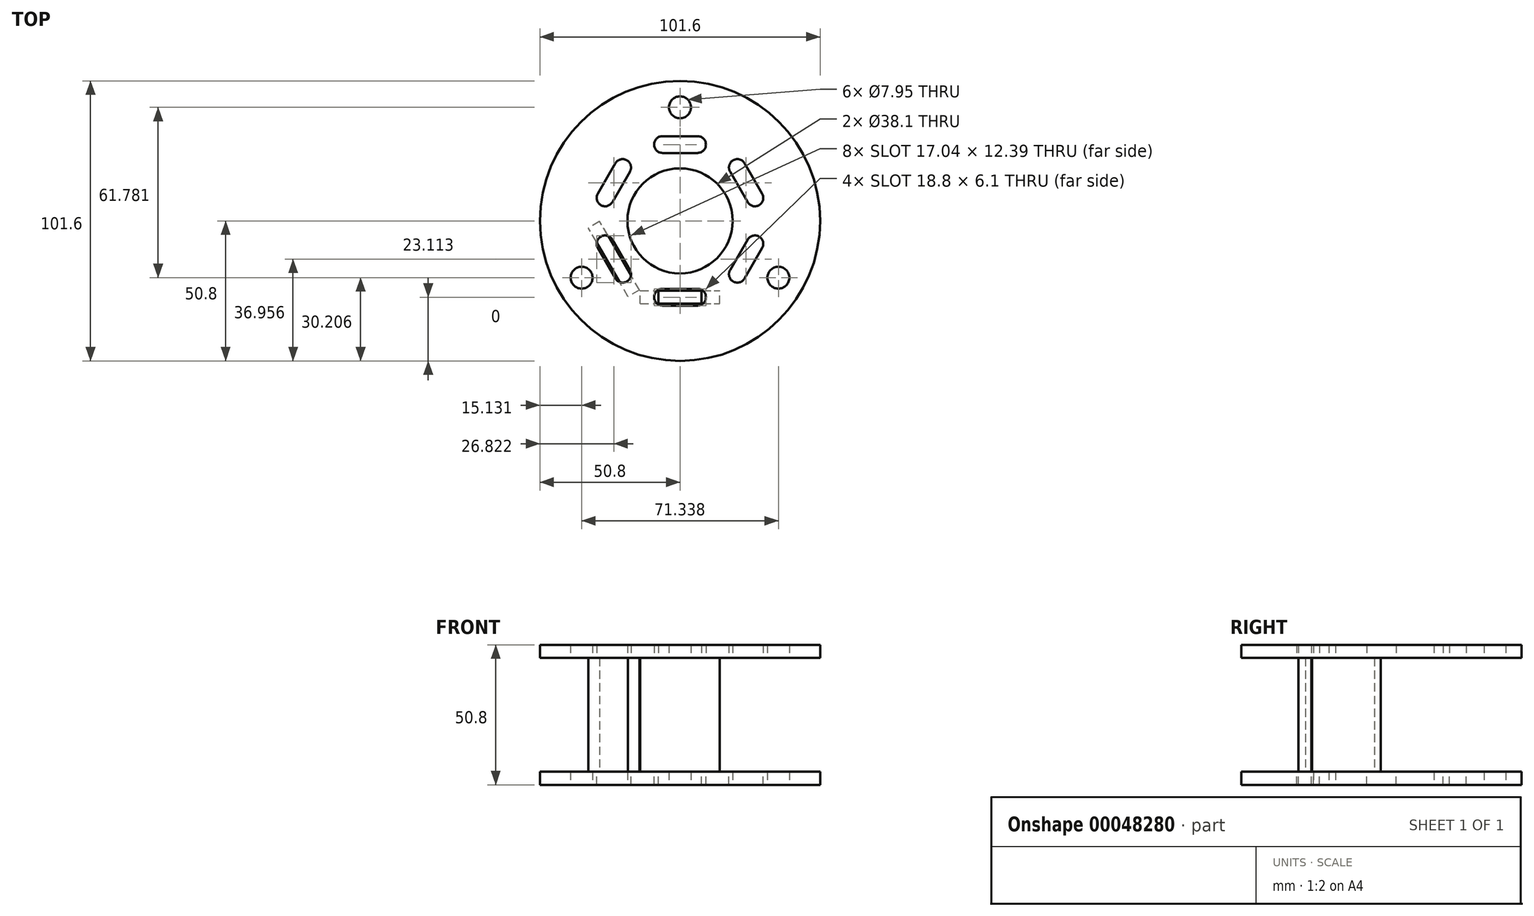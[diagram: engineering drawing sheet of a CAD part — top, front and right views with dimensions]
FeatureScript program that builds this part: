
annotation { "Feature Type Name" : "Feature", "Feature Type Description" : "" }
export const myFeature = defineFeature(function(context is Context, id is Id, definition is map)
    precondition{}
    {
        {
            var Q0;
            Q0=qCreatedBy(makeId("Top.planeOp"),FACE);
            var sketch = newSketch(context, id + "F0", { "sketchPlane" : qUnion([Q0])});
            skCircle(sketch, "E0", {"center": v(0, 0) * mm, "radius": 19.05 * mm});
            skCircle(sketch, "E1", {"center": v(0, 0) * mm, "radius": 50.8 * mm});
            skCircle(sketch, "E2", {"center": v(0, 41.19) * mm, "radius": 3.98 * mm});
            skCircle(sketch, "E3.1.0", {"center": v(-35.67, -20.6) * mm, "radius": 3.98 * mm});
            skCircle(sketch, "E3.2.0", {"center": v(35.67, -20.6) * mm, "radius": 3.98 * mm});
            skSolve(sketch);
        }
        {
            var Q0;
            Q0 = qSketchRegion(id + "F0", true);
            extrude(context, id + "F1", {"entities" : qUnion([Q0]), "depth" : 4.75 * mm});
        }
        {
            var Q0;
            Q0=makeQuery(id+"F1.opExtrude","CAP_FACE",FACE,{"disambiguationData":[OSD([sQuery(id+"F0.wireOp",EDGE,"E0"),sQuery(id+"F0.wireOp",EDGE,"E1"),sQuery(id+"F0.wireOp",EDGE,"E2"),sQuery(id+"F0.wireOp",EDGE,"E3.1.0"),sQuery(id+"F0.wireOp",EDGE,"E3.2.0")])],"isStart":false});
            var sketch = newSketch(context, id + "F2", { "sketchPlane" : qUnion([Q0])});
            skCircle(sketch, "E4.cCircle", {"center": v(0, 0) * mm, "radius": 27.69 * mm, "construction": true});
            skLineSegment(sketch, "E4.0", {"start": v(15.99, -27.69) * mm, "end": v(-15.99, -27.69) * mm, "construction": true});
            skLineSegment(sketch, "E4.1", {"start": v(-15.99, -27.69) * mm, "end": v(-31.97, 0) * mm, "construction": true});
            skLineSegment(sketch, "E4.2", {"start": v(-31.97, 0) * mm, "end": v(-15.99, 27.69) * mm, "construction": true});
            skLineSegment(sketch, "E4.3", {"start": v(-15.99, 27.69) * mm, "end": v(15.99, 27.69) * mm, "construction": true});
            skLineSegment(sketch, "E4.4", {"start": v(15.99, 27.69) * mm, "end": v(31.97, 0) * mm, "construction": true});
            skLineSegment(sketch, "E4.5", {"start": v(31.97, 0) * mm, "end": v(15.99, -27.69) * mm, "construction": true});
            skPoint(sketch, "E4.0.midPoint", {"position": v(0, -27.69) * mm});
            skSolve(sketch);
        }
        {
            var Q0;
            Q0=makeQuery(id+"F2.imprint","IMPRINT",FACE,{"disambiguationData":[TD([[makeQuery(id+"F2.imprint","IMPRINT",EDGE,{"derivedFrom":makeQuery(id+"F1.opExtrude","CAP_EDGE",EDGE,{"disambiguationData":[OSD([sQuery(id+"F0.wireOp",EDGE,"E0")])],"isStart":false})}),-1.0]])]});
            var sketch = newSketch(context, id + "F3", { "sketchPlane" : qUnion([Q0])});
            skPoint(sketch, "E5.0", {"position": v(0, -27.69) * mm});
            skPoint(sketch, "E5.1", {"position": v(23.98, 13.84) * mm});
            skPoint(sketch, "E5.2", {"position": v(0, 27.69) * mm});
            skPoint(sketch, "E5.3", {"position": v(-23.98, 13.84) * mm});
            skPoint(sketch, "E5.4", {"position": v(-23.98, -13.84) * mm});
            skPoint(sketch, "E5.5", {"position": v(23.98, -13.84) * mm});
            skLineSegment(sketch, "E6", {"start": v(-6.35, 27.69) * mm, "end": v(6.35, 27.69) * mm});
            skLineSegment(sketch, "E7", {"start": v(27.15, 8.34) * mm, "end": v(20.8, 19.34) * mm});
            skLineSegment(sketch, "E8", {"start": v(27.15, -8.34) * mm, "end": v(20.8, -19.34) * mm});
            skLineSegment(sketch, "E9", {"start": v(6.35, -27.69) * mm, "end": v(-6.35, -27.69) * mm});
            skLineSegment(sketch, "E10", {"start": v(-20.8, -19.34) * mm, "end": v(-27.15, -8.34) * mm});
            skLineSegment(sketch, "E11", {"start": v(-27.15, 8.34) * mm, "end": v(-20.8, 19.34) * mm});
            skArc(sketch, "E12.0.startCap", {"start": v(-6.35, 24.64) * mm, "mid": v(-9.4, 27.69) * mm, "end": v(-6.35, 30.73) * mm});
            skArc(sketch, "E12.0.endCap", {"start": v(6.35, 30.73) * mm, "mid": v(9.4, 27.69) * mm, "end": v(6.35, 24.64) * mm});
            skLineSegment(sketch, "E12.0.left", {"start": v(-6.35, 30.73) * mm, "end": v(6.35, 30.73) * mm});
            skLineSegment(sketch, "E12.0.right", {"start": v(-6.35, 24.64) * mm, "end": v(6.35, 24.64) * mm});
            skArc(sketch, "E12.1.startCap", {"start": v(29.8, 9.87) * mm, "mid": v(28.68, 5.7) * mm, "end": v(24.51, 6.82) * mm});
            skArc(sketch, "E12.1.endCap", {"start": v(18.16, 17.82) * mm, "mid": v(19.28, 21.98) * mm, "end": v(23.44, 20.87) * mm});
            skLineSegment(sketch, "E12.1.left", {"start": v(24.51, 6.82) * mm, "end": v(18.16, 17.82) * mm});
            skLineSegment(sketch, "E12.1.right", {"start": v(29.8, 9.87) * mm, "end": v(23.44, 20.87) * mm});
            skArc(sketch, "E12.2.startCap", {"start": v(24.51, -6.82) * mm, "mid": v(28.68, -5.7) * mm, "end": v(29.8, -9.87) * mm});
            skArc(sketch, "E12.2.endCap", {"start": v(23.44, -20.87) * mm, "mid": v(19.28, -21.98) * mm, "end": v(18.16, -17.82) * mm});
            skLineSegment(sketch, "E12.2.left", {"start": v(29.8, -9.87) * mm, "end": v(23.44, -20.87) * mm});
            skLineSegment(sketch, "E12.2.right", {"start": v(24.51, -6.82) * mm, "end": v(18.16, -17.82) * mm});
            skArc(sketch, "E12.3.startCap", {"start": v(6.35, -24.64) * mm, "mid": v(9.4, -27.69) * mm, "end": v(6.35, -30.73) * mm});
            skArc(sketch, "E12.3.endCap", {"start": v(-6.35, -30.73) * mm, "mid": v(-9.4, -27.69) * mm, "end": v(-6.35, -24.64) * mm});
            skLineSegment(sketch, "E12.3.left", {"start": v(6.35, -30.73) * mm, "end": v(-6.35, -30.73) * mm});
            skLineSegment(sketch, "E12.3.right", {"start": v(6.35, -24.64) * mm, "end": v(-6.35, -24.64) * mm});
            skArc(sketch, "E12.4.startCap", {"start": v(-18.16, -17.82) * mm, "mid": v(-19.28, -21.98) * mm, "end": v(-23.44, -20.87) * mm});
            skArc(sketch, "E12.4.endCap", {"start": v(-29.8, -9.87) * mm, "mid": v(-28.68, -5.7) * mm, "end": v(-24.51, -6.82) * mm});
            skLineSegment(sketch, "E12.4.left", {"start": v(-23.44, -20.87) * mm, "end": v(-29.8, -9.87) * mm});
            skLineSegment(sketch, "E12.4.right", {"start": v(-18.16, -17.82) * mm, "end": v(-24.51, -6.82) * mm});
            skArc(sketch, "E12.5.startCap", {"start": v(-24.51, 6.82) * mm, "mid": v(-28.68, 5.7) * mm, "end": v(-29.8, 9.87) * mm});
            skArc(sketch, "E12.5.endCap", {"start": v(-23.44, 20.87) * mm, "mid": v(-19.28, 21.98) * mm, "end": v(-18.16, 17.82) * mm});
            skLineSegment(sketch, "E12.5.left", {"start": v(-29.8, 9.87) * mm, "end": v(-23.44, 20.87) * mm});
            skLineSegment(sketch, "E12.5.right", {"start": v(-24.51, 6.82) * mm, "end": v(-18.16, 17.82) * mm});
            skSolve(sketch);
        }
        {
            var Q0;
            Q0 = qSketchRegion(id + "F3", true);
            extrude(context, id + "F4", {"entities" : qUnion([Q0]), "operationType" : NewBodyOperationType.REMOVE, "oppositeDirection" : true, "depth" : 25.4 * mm});
        }
        {
            var Q0;
            Q0=makeQuery(id+"F2.imprint","IMPRINT",FACE,{"disambiguationData":[TD([[makeQuery(id+"F2.imprint","IMPRINT",EDGE,{"derivedFrom":makeQuery(id+"F1.opExtrude","CAP_EDGE",EDGE,{"disambiguationData":[OSD([sQuery(id+"F0.wireOp",EDGE,"E0")])],"isStart":false})}),-1.0]])]});
            var sketch = newSketch(context, id + "F5", { "sketchPlane" : qUnion([Q0])});
            skPoint(sketch, "E13.0", {"position": v(0, -27.69) * mm});
            skPoint(sketch, "E13.1", {"position": v(23.98, -13.84) * mm});
            skPoint(sketch, "E13.2", {"position": v(23.98, 13.84) * mm});
            skPoint(sketch, "E13.3", {"position": v(0, 27.69) * mm});
            skPoint(sketch, "E13.4", {"position": v(-23.98, 13.84) * mm});
            skPoint(sketch, "E13.5", {"position": v(-23.98, -13.84) * mm});
            skLineSegment(sketch, "E14.bottom", {"start": v(-14.4, -30.06) * mm, "end": v(14.4, -30.06) * mm});
            skLineSegment(sketch, "E14.top", {"start": v(-14.4, -25.31) * mm, "end": v(14.4, -25.31) * mm});
            skLineSegment(sketch, "E14.left", {"start": v(-14.4, -30.06) * mm, "end": v(-14.4, -25.31) * mm});
            skLineSegment(sketch, "E14.right", {"start": v(14.4, -30.06) * mm, "end": v(14.4, -25.31) * mm});
            skPoint(sketch, "E15.0", {"position": v(-15.99, -27.69) * mm});
            skLineSegment(sketch, "E16.bottom", {"start": v(-14.72, -25.12) * mm, "end": v(-18.84, -27.5) * mm});
            skLineSegment(sketch, "E16.top", {"start": v(-29.12, -0.19) * mm, "end": v(-33.23, -2.56) * mm});
            skLineSegment(sketch, "E16.left", {"start": v(-14.72, -25.12) * mm, "end": v(-29.12, -0.19) * mm});
            skLineSegment(sketch, "E16.right", {"start": v(-18.84, -27.5) * mm, "end": v(-33.23, -2.56) * mm});
            skSolve(sketch);
        }
        {
            var Q0;
            Q0 = qSketchRegion(id + "F5", true);
            extrude(context, id + "F6", {"entities" : qUnion([Q0]), "depth" : 41.3 * mm});
        }
        {
            var Q0;
            Q0=makeQuery(id+"F6.opExtrude","CAP_FACE",FACE,{"disambiguationData":[OSD([sQuery(id+"F5.wireOp",EDGE,"E14.bottom"),sQuery(id+"F5.wireOp",EDGE,"E14.top"),sQuery(id+"F5.wireOp",EDGE,"E14.left"),sQuery(id+"F5.wireOp",EDGE,"E14.right")])],"isStart":true});
            var sketch = newSketch(context, id + "F7", { "sketchPlane" : qUnion([Q0])});
            skPoint(sketch, "E17.0", {"position": v(9.4, 27.69) * mm});
            skPoint(sketch, "E17.1", {"position": v(-9.4, 27.69) * mm});
            skLineSegment(sketch, "E18", {"start": v(-7.81, 27.69) * mm, "end": v(7.81, 27.69) * mm, "construction": true});
            skPoint(sketch, "E19", {"position": v(0, 27.69) * mm});
            skLineSegment(sketch, "E20.bottom", {"start": v(7.81, 25.31) * mm, "end": v(-7.81, 25.31) * mm});
            skLineSegment(sketch, "E20.top", {"start": v(7.81, 30.06) * mm, "end": v(-7.81, 30.06) * mm});
            skLineSegment(sketch, "E20.left", {"start": v(7.81, 25.31) * mm, "end": v(7.81, 30.06) * mm});
            skLineSegment(sketch, "E20.right", {"start": v(-7.81, 25.31) * mm, "end": v(-7.81, 30.06) * mm});
            skSolve(sketch);
        }
        {
            var Q0;
            Q0 = qSketchRegion(id + "F7", true);
            extrude(context, id + "F8", {"entities" : qUnion([Q0]), "operationType" : NewBodyOperationType.ADD, "depth" : 4.75 * mm});
        }
        {
            var Q0;
            Q0=makeQuery(id+"F6.opExtrude","CAP_FACE",FACE,{"disambiguationData":[OSD([sQuery(id+"F5.wireOp",EDGE,"E14.bottom"),sQuery(id+"F5.wireOp",EDGE,"E14.top"),sQuery(id+"F5.wireOp",EDGE,"E14.left"),sQuery(id+"F5.wireOp",EDGE,"E14.right")])],"isStart":false});
            var sketch = newSketch(context, id + "F9", { "sketchPlane" : qUnion([Q0])});
            skLineSegment(sketch, "E21.0", {"start": v(29.8, -9.87) * mm, "end": v(23.44, -20.87) * mm});
            skArc(sketch, "E21.1", {"start": v(24.51, -6.82) * mm, "mid": v(28.68, -5.7) * mm, "end": v(29.8, -9.87) * mm});
            skLineSegment(sketch, "E21.2", {"start": v(24.51, -6.82) * mm, "end": v(18.16, -17.82) * mm});
            skArc(sketch, "E21.3", {"start": v(23.44, -20.87) * mm, "mid": v(19.28, -21.98) * mm, "end": v(18.16, -17.82) * mm});
            skLineSegment(sketch, "E21.4", {"start": v(24.51, 6.82) * mm, "end": v(18.16, 17.82) * mm});
            skArc(sketch, "E21.5", {"start": v(29.8, 9.87) * mm, "mid": v(28.68, 5.7) * mm, "end": v(24.51, 6.82) * mm});
            skLineSegment(sketch, "E21.6", {"start": v(29.8, 9.87) * mm, "end": v(23.44, 20.87) * mm});
            skArc(sketch, "E21.7", {"start": v(18.16, 17.82) * mm, "mid": v(19.28, 21.98) * mm, "end": v(23.44, 20.87) * mm});
            skArc(sketch, "E21.8", {"start": v(6.35, 30.73) * mm, "mid": v(9.4, 27.69) * mm, "end": v(6.35, 24.64) * mm});
            skLineSegment(sketch, "E21.9", {"start": v(-6.35, 24.64) * mm, "end": v(6.35, 24.64) * mm});
            skLineSegment(sketch, "E21.10", {"start": v(-6.35, 30.73) * mm, "end": v(6.35, 30.73) * mm});
            skArc(sketch, "E21.11", {"start": v(-6.35, 24.64) * mm, "mid": v(-9.4, 27.69) * mm, "end": v(-6.35, 30.73) * mm});
            skArc(sketch, "E21.12", {"start": v(-23.44, 20.87) * mm, "mid": v(-19.28, 21.98) * mm, "end": v(-18.16, 17.82) * mm});
            skLineSegment(sketch, "E21.13", {"start": v(-24.51, 6.82) * mm, "end": v(-18.16, 17.82) * mm});
            skLineSegment(sketch, "E21.14", {"start": v(-29.8, 9.87) * mm, "end": v(-23.44, 20.87) * mm});
            skArc(sketch, "E21.15", {"start": v(-24.51, 6.82) * mm, "mid": v(-28.68, 5.7) * mm, "end": v(-29.8, 9.87) * mm});
            skLineSegment(sketch, "E22.0", {"start": v(6.35, -30.73) * mm, "end": v(-6.35, -30.73) * mm});
            skArc(sketch, "E22.1", {"start": v(-6.35, -30.73) * mm, "mid": v(-9.4, -27.69) * mm, "end": v(-6.35, -24.64) * mm});
            skArc(sketch, "E22.2", {"start": v(6.35, -24.64) * mm, "mid": v(9.4, -27.69) * mm, "end": v(6.35, -30.73) * mm});
            skLineSegment(sketch, "E22.3", {"start": v(6.35, -24.64) * mm, "end": v(-6.35, -24.64) * mm});
            skArc(sketch, "E22.4", {"start": v(-18.16, -17.82) * mm, "mid": v(-19.28, -21.98) * mm, "end": v(-23.44, -20.87) * mm});
            skLineSegment(sketch, "E22.5", {"start": v(-18.16, -17.82) * mm, "end": v(-24.51, -6.82) * mm});
            skLineSegment(sketch, "E22.6", {"start": v(-23.44, -20.87) * mm, "end": v(-29.8, -9.87) * mm});
            skArc(sketch, "E22.7", {"start": v(-29.8, -9.87) * mm, "mid": v(-28.68, -5.7) * mm, "end": v(-24.51, -6.82) * mm});
            skCircle(sketch, "E22.8", {"center": v(-35.67, -20.6) * mm, "radius": 3.98 * mm});
            skCircle(sketch, "E22.9", {"center": v(0, 0) * mm, "radius": 19.05 * mm});
            skCircle(sketch, "E22.10", {"center": v(35.67, -20.6) * mm, "radius": 3.98 * mm});
            skCircle(sketch, "E22.11", {"center": v(0, 41.19) * mm, "radius": 3.98 * mm});
            skCircle(sketch, "E22.12", {"center": v(0, 0) * mm, "radius": 50.8 * mm});
            skSolve(sketch);
        }
        {
            var Q0;
            Q0 = qSketchRegion(id + "F9", true);
            extrude(context, id + "F10", {"entities" : qUnion([Q0]), "depth" : 4.75 * mm});
        }
        {
            var Q0;
            Q0=makeQuery(id+"F6.opExtrude","CAP_FACE",FACE,{"disambiguationData":[OSD([sQuery(id+"F5.wireOp",EDGE,"E14.bottom"),sQuery(id+"F5.wireOp",EDGE,"E14.top"),sQuery(id+"F5.wireOp",EDGE,"E14.left"),sQuery(id+"F5.wireOp",EDGE,"E14.right")])],"isStart":false});
            var sketch = newSketch(context, id + "F11", { "sketchPlane" : qUnion([Q0])});
            skLineSegment(sketch, "E23.0.0", {"start": v(-7.81, -25.31) * mm, "end": v(7.81, -25.31) * mm});
            skLineSegment(sketch, "E23.0.1", {"start": v(7.81, -25.31) * mm, "end": v(7.81, -30.06) * mm});
            skLineSegment(sketch, "E23.0.2", {"start": v(7.81, -30.06) * mm, "end": v(-7.81, -30.06) * mm});
            skLineSegment(sketch, "E23.0.3", {"start": v(-7.81, -30.06) * mm, "end": v(-7.81, -25.31) * mm});
            skSolve(sketch);
        }
        {
            var Q0;
            Q0 = qSketchRegion(id + "F11", true);
            extrude(context, id + "F12", {"entities" : qUnion([Q0]), "operationType" : NewBodyOperationType.ADD, "depth" : 4.75 * mm});
        }
    });
